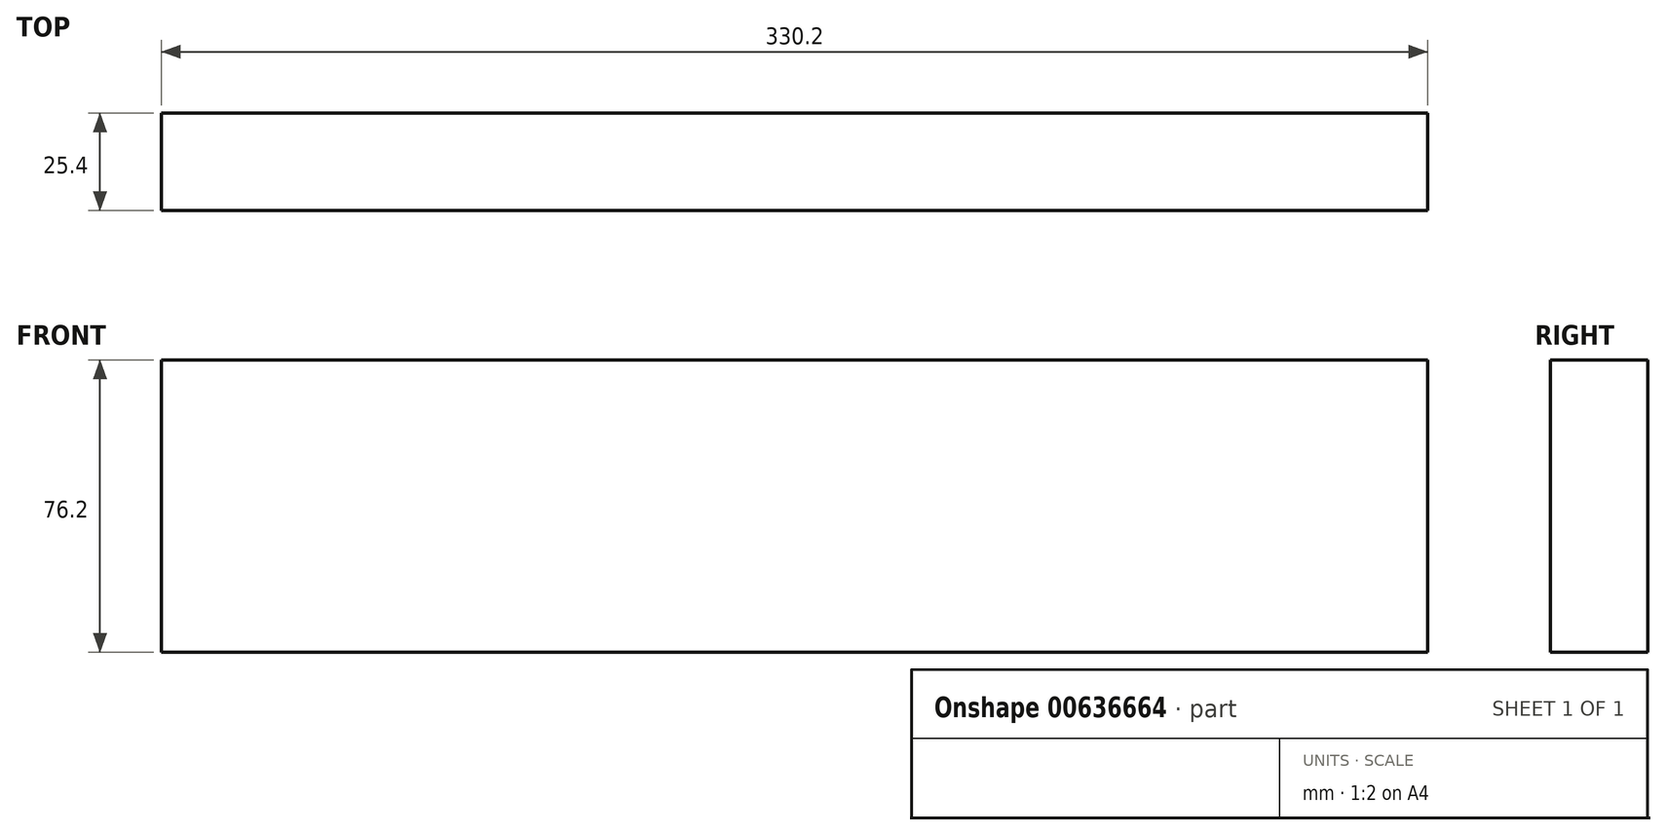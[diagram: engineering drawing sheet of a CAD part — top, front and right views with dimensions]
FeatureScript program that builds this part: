
annotation { "Feature Type Name" : "Feature", "Feature Type Description" : "" }
export const myFeature = defineFeature(function(context is Context, id is Id, definition is map)
    precondition{}
    {
        {
            var Q0;
            Q0=qCreatedBy(makeId("Front.planeOp"),FACE);
            var sketch = newSketch(context, id + "F0", { "sketchPlane" : qUnion([Q0])});
            skLineSegment(sketch, "E0.bottom", {"start": v(-146.26, 21.94) * mm, "end": v(183.94, 21.94) * mm});
            skLineSegment(sketch, "E0.top", {"start": v(-146.26, -54.26) * mm, "end": v(183.94, -54.26) * mm});
            skLineSegment(sketch, "E0.left", {"start": v(-146.26, 21.94) * mm, "end": v(-146.26, -54.26) * mm});
            skLineSegment(sketch, "E0.right", {"start": v(183.94, 21.94) * mm, "end": v(183.94, -54.26) * mm});
            skSolve(sketch);
        }
        {
            var Q0;
            Q0=makeQuery(id+"F0.imprint","IMPRINT",FACE,{"disambiguationData":[TD([[makeQuery(id+"F0.imprint","IMPRINT",EDGE,{"derivedFrom":sQuery(id+"F0.wireOp",EDGE,"E0.bottom")}),-1.0]])]});
            extrude(context, id + "F1", {"entities" : qUnion([Q0]), "depth" : 25.4 * mm, "offsetDistance" : 25.4 * mm});
        }
    });
